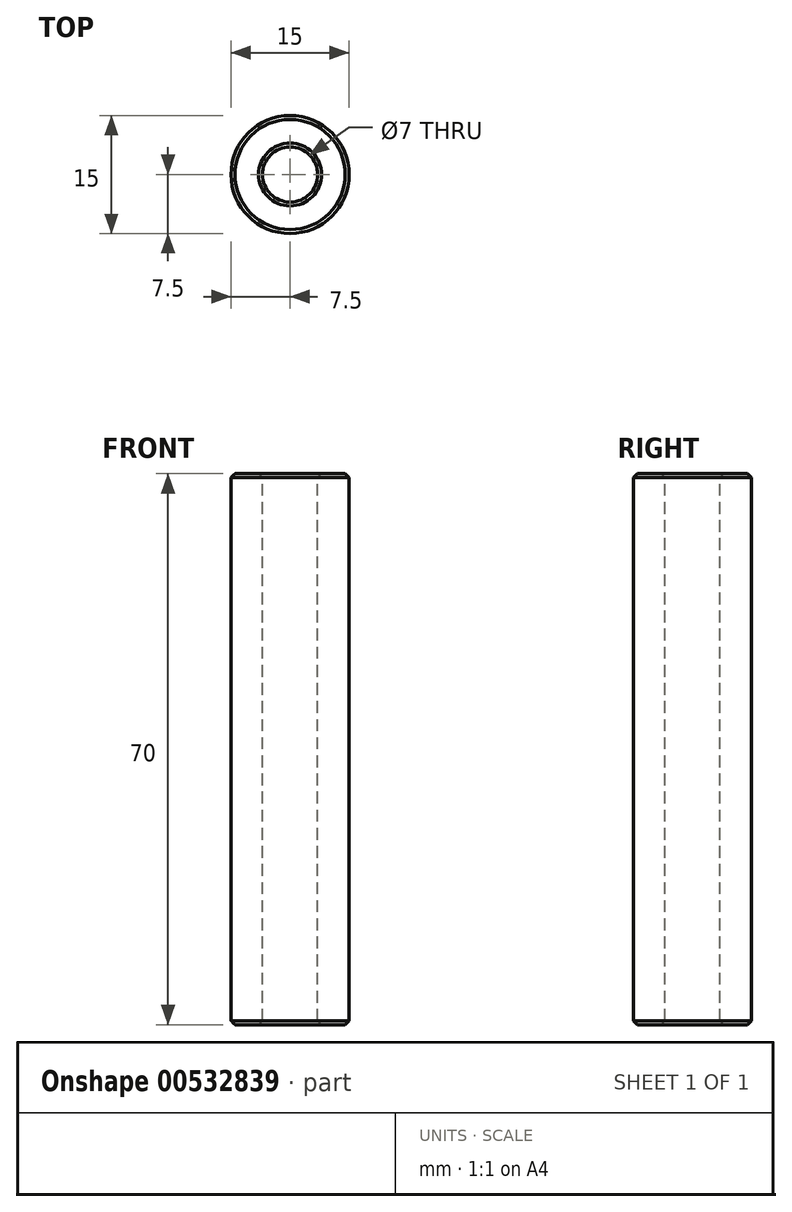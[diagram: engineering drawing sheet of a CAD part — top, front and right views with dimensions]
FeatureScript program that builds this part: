
annotation { "Feature Type Name" : "Feature", "Feature Type Description" : "" }
export const myFeature = defineFeature(function(context is Context, id is Id, definition is map)
    precondition{}
    {
        {
            var Q0;
            Q0=qCreatedBy(makeId("Front.planeOp"),FACE);
            var sketch = newSketch(context, id + "F0", { "sketchPlane" : qUnion([Q0])});
            skLineSegment(sketch, "E0.bottom", {"start": v(-7.5, 35) * mm, "end": v(-3.5, 35) * mm});
            skLineSegment(sketch, "E0.top", {"start": v(-7.5, -35) * mm, "end": v(-3.5, -35) * mm});
            skLineSegment(sketch, "E0.left", {"start": v(-7.5, 35) * mm, "end": v(-7.5, -35) * mm});
            skLineSegment(sketch, "E0.right", {"start": v(-3.5, 35) * mm, "end": v(-3.5, -35) * mm});
            skLineSegment(sketch, "E1", {"start": v(0, 42.97) * mm, "end": v(0, -42.97) * mm, "construction": true});
            skSolve(sketch);
        }
        {
            var Q0;
            Q0=makeQuery(id+"F0.imprint","IMPRINT",FACE,{"disambiguationData":[TD([[makeQuery(id+"F0.imprint","IMPRINT",EDGE,{"derivedFrom":sQuery(id+"F0.wireOp",EDGE,"E0.bottom")}),-1.0]])]});
            var Q1;
            Q1=sQuery(id+"F0.wireOp",EDGE,"E1");
            revolve(context, id + "F1", {"entities" : qUnion([Q0]), "axis" : qUnion([Q1]), "revolveType" : RevolveType.FULL});
        }
        {
            var Q0;
            Q0=makeQuery(id+"F1.opRevolve","SWEPT_FACE",FACE,{"disambiguationData":[OSD([sQuery(id+"F0.wireOp",EDGE,"E0.bottom")])]});
            var Q1;
            Q1=makeQuery(id+"F1.opRevolve","SWEPT_FACE",FACE,{"disambiguationData":[OSD([sQuery(id+"F0.wireOp",EDGE,"E0.top")])]});
            chamfer(context, id + "F2", {"entities" : qUnion([Q0, Q1]), "width" : 0.5 * mm, "tangentPropagation" : true});
        }
    });
